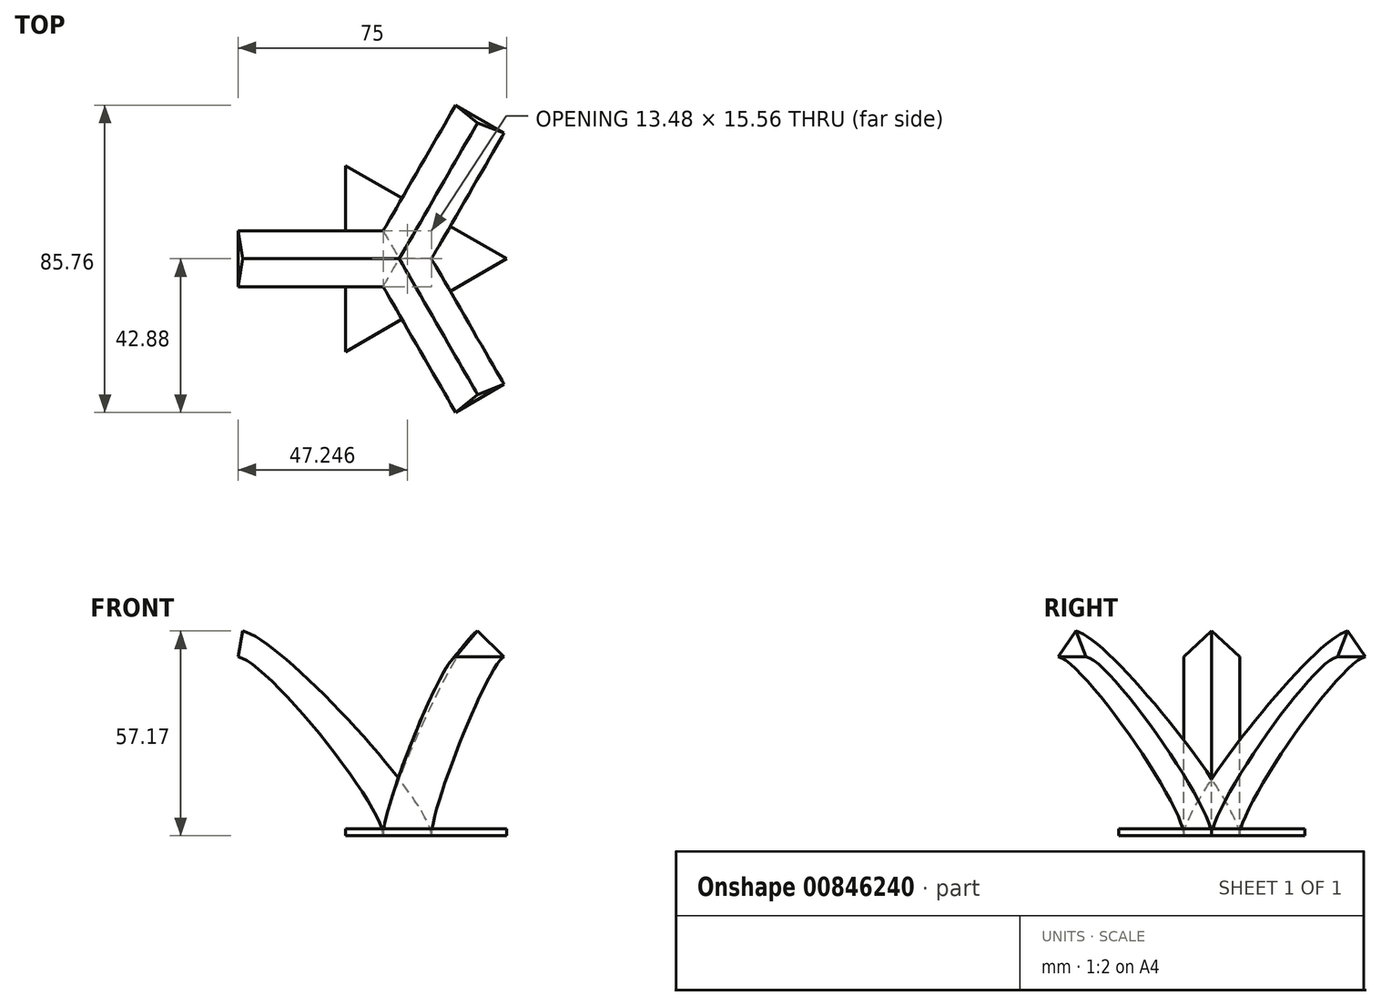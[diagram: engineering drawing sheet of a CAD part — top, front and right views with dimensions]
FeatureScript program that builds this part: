
annotation { "Feature Type Name" : "Feature", "Feature Type Description" : "" }
export const myFeature = defineFeature(function(context is Context, id is Id, definition is map)
    precondition{}
    {
        {
            var Q0;
            Q0=qCreatedBy(makeId("Top.planeOp"),FACE);
            var sketch = newSketch(context, id + "F0", { "sketchPlane" : qUnion([Q0])});
            skCircle(sketch, "E0", {"center": v(0, 0) * mm, "radius": 45 * mm, "construction": true});
            skLineSegment(sketch, "E1", {"start": v(100.05, 0) * mm, "end": v(-50, 0) * mm, "construction": true});
            skPoint(sketch, "E2.center", {"position": v(-45, 0) * mm});
            skLineSegment(sketch, "E3", {"start": v(-45, 68.85) * mm, "end": v(-45, -68.85) * mm});
            skLineSegment(sketch, "E4.1.0", {"start": v(-37.13, -73.4) * mm, "end": v(82.13, -4.55) * mm});
            skLineSegment(sketch, "E4.2.0", {"start": v(82.13, 4.55) * mm, "end": v(-37.13, 73.4) * mm});
            skLineSegment(sketch, "E5", {"start": v(-15, 25.98) * mm, "end": v(-15, -25.98) * mm});
            skPoint(sketch, "E6", {"position": v(-15, 0) * mm});
            skLineSegment(sketch, "E7.1.0", {"start": v(-50.02, 86.64) * mm, "end": v(25, -43.3) * mm, "construction": true});
            skLineSegment(sketch, "E7.2.0", {"start": v(-50.02, -86.64) * mm, "end": v(25, 43.3) * mm, "construction": true});
            skLineSegment(sketch, "E8.1.0", {"start": v(-15, -25.98) * mm, "end": v(30, 0) * mm});
            skLineSegment(sketch, "E8.2.0", {"start": v(30, 0) * mm, "end": v(-15, 25.98) * mm});
            skLineSegment(sketch, "E9.0", {"start": v(8.99, 0) * mm, "end": v(-4.5, 7.78) * mm});
            skLineSegment(sketch, "E9.1", {"start": v(-4.5, -7.78) * mm, "end": v(8.99, 0) * mm});
            skLineSegment(sketch, "E9.2", {"start": v(-4.5, 7.78) * mm, "end": v(-4.5, -7.78) * mm});
            skCircle(sketch, "E10", {"center": v(0, 0) * mm, "radius": 30 * mm, "construction": true});
            skSolve(sketch);
        }
        {
            var Q0;
            Q0=makeQuery(id+"F0.imprint","IMPRINT",FACE,{"disambiguationData":[TD([[makeQuery(id+"F0.imprint","IMPRINT",EDGE,{"derivedFrom":sQuery(id+"F0.wireOp",EDGE,"E5")}),1.0]])]});
            extrude(context, id + "F1", {"entities" : qUnion([Q0]), "depth" : 2 * mm, "offsetDistance" : 25 * mm});
        }
        {
            var Q0;
            Q0=qCreatedBy(makeId("Top.planeOp"),FACE);
            cPlane(context, id + "F2", {"entities" : qUnion([Q0]), "cplaneType" : CPlaneType.OFFSET, "offset" : 50 * mm, "width" : 150 * mm, "height" : 150 * mm});
        }
        {
            var Q0;
            Q0=qCreatedBy(id+"F2.planeOp",FACE);
            var sketch = newSketch(context, id + "F3", { "sketchPlane" : qUnion([Q0])});
            skLineSegment(sketch, "E11.0", {"start": v(-45, 68.85) * mm, "end": v(-45, -68.85) * mm});
            skLineSegment(sketch, "E12.0.0", {"start": v(8.99, 0) * mm, "end": v(-4.5, 7.78) * mm});
            skLineSegment(sketch, "E12.0.1", {"start": v(-4.5, 7.78) * mm, "end": v(-4.5, -7.78) * mm});
            skLineSegment(sketch, "E12.0.2", {"start": v(-4.5, -7.78) * mm, "end": v(8.99, 0) * mm});
            skSolve(sketch);
        }
        {
            var Q0;
            Q0=sQuery(id+"F3.wireOp",EDGE,"E11.0");
            cPlane(context, id + "F4", {"entities" : qUnion([Q0]), "cplaneType" : CPlaneType.LINE_ANGLE, "offset" : 25 * mm, "angle" : 80 * degree, "width" : 150 * mm, "height" : 150 * mm});
        }
        {
            var Q0;
            Q0=qCreatedBy(id+"F4.planeOp",FACE);
            var sketch = newSketch(context, id + "F5", { "sketchPlane" : qUnion([Q0])});
            skLineSegment(sketch, "E13.0", {"start": v(68.85, 41.43) * mm, "end": v(-68.85, 41.43) * mm});
            skLineSegment(sketch, "E14", {"start": v(0, 48.7) * mm, "end": v(7.8, 41.43) * mm});
            skPoint(sketch, "E14.startSnap0", {"position": v(0, 41.43) * mm});
            skLineSegment(sketch, "E15", {"start": v(7.8, 41.43) * mm, "end": v(-7.8, 41.43) * mm});
            skLineSegment(sketch, "E16", {"start": v(-7.8, 41.43) * mm, "end": v(0, 48.7) * mm});
            skSolve(sketch);
        }
        {
            var Q1;
            Q1=makeQuery(id+"F0.imprint","IMPRINT",FACE,{"disambiguationData":[TD([[makeQuery(id+"F0.imprint","IMPRINT",EDGE,{"derivedFrom":sQuery(id+"F0.wireOp",EDGE,"E9.0")}),1.0]])]});
            var Q2;
            Q2=makeQuery(id+"F5.imprint","IMPRINT",FACE,{"disambiguationData":[TD([[makeQuery(id+"F5.imprint","IMPRINT",EDGE,{"derivedFrom":sQuery(id+"F5.wireOp",EDGE,"E14")}),-1.0]])]});
            loft(context, id + "F6", {"startCondition" : LoftEndDerivativeType.NORMAL_TO_PROFILE, "startMagnitude" : 0.5, "endCondition" : LoftEndDerivativeType.NORMAL_TO_PROFILE, "endMagnitude" : 0.5, "sheetProfilesArray" : [{ "sheetProfileEntities" : qUnion([Q1]) }, { "sheetProfileEntities" : qUnion([Q2]) }]});
        }
        {
            var Q0;
            Q0=qCreatedBy(makeId("Right.planeOp"),FACE);
            var sketch = newSketch(context, id + "F7", { "sketchPlane" : qUnion([Q0])});
            skLineSegment(sketch, "E17", {"start": v(0, -40.85) * mm, "end": v(0, 0) * mm, "construction": true});
            skSolve(sketch);
        }
        {
            var Q0;
            Q0=makeQuery(id+"F6.opLoft","SWEPT_BODY",BODY,{"disambiguationData":[OSD([makeQuery(id+"F0.imprint","IMPRINT",FACE,{"disambiguationData":[TD([[makeQuery(id+"F0.imprint","IMPRINT",EDGE,{"derivedFrom":sQuery(id+"F0.wireOp",EDGE,"E9.0")}),1.0]])]}),makeQuery(id+"F5.imprint","IMPRINT",FACE,{"disambiguationData":[TD([[makeQuery(id+"F5.imprint","IMPRINT",EDGE,{"derivedFrom":sQuery(id+"F5.wireOp",EDGE,"E14")}),-1.0]])]})])]});
            var Q1;
            Q1=sQuery(id+"F7.wireOp",EDGE,"E17");
            circularPattern(context, id + "F8", {"entities" : qUnion([Q0]), "axis" : qUnion([Q1]), "angle" : 360 * degree, "instanceCount" : 3, "equalSpace" : true});
        }
    });
